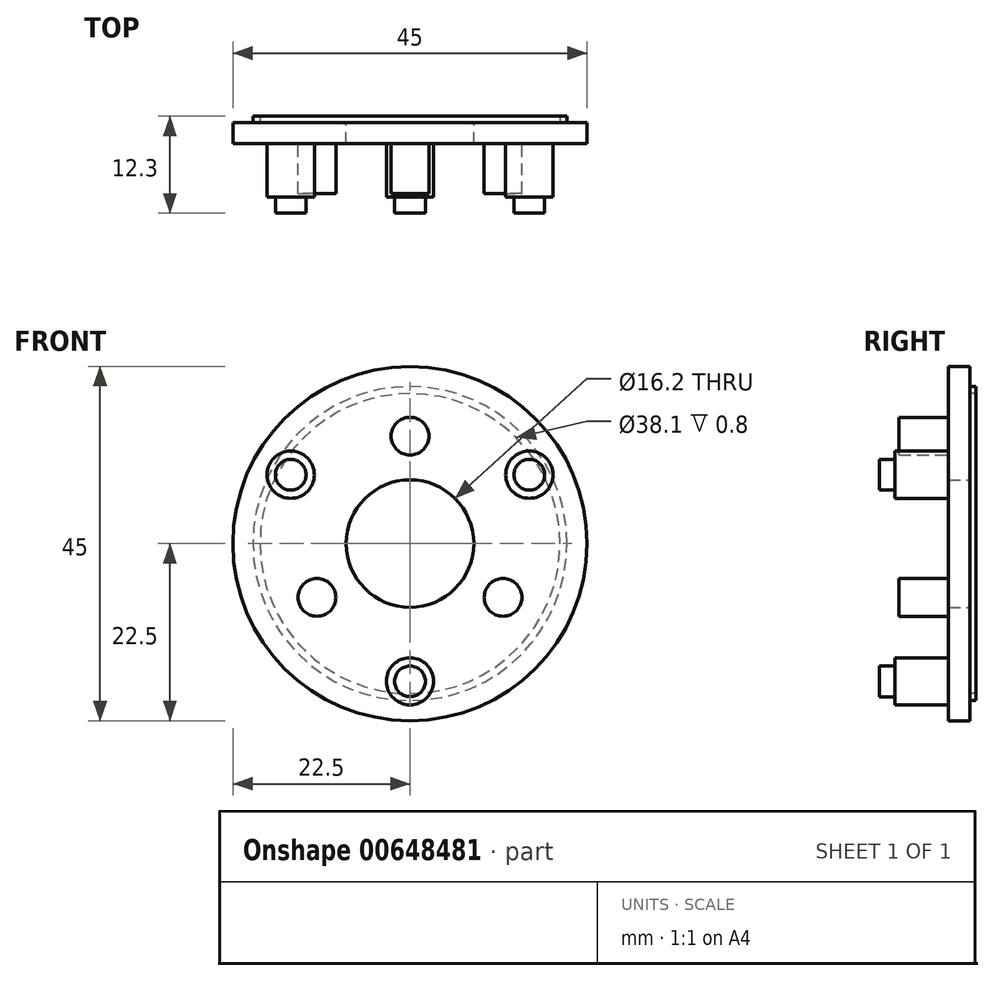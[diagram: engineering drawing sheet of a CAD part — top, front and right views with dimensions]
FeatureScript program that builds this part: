
annotation { "Feature Type Name" : "Feature", "Feature Type Description" : "" }
export const myFeature = defineFeature(function(context is Context, id is Id, definition is map)
    precondition{}
    {
        {
            var Q0;
            Q0=qCreatedBy(makeId("Front.planeOp"),FACE);
            var sketch = newSketch(context, id + "F0", { "sketchPlane" : qUnion([Q0])});
            skCircle(sketch, "E0", {"center": v(0, 0) * mm, "radius": 22.5 * mm});
            skCircle(sketch, "E1", {"center": v(0, 0) * mm, "radius": 8.1 * mm});
            skSolve(sketch);
        }
        {
            var Q0;
            Q0 = qSketchRegion(id + "F0", true);
            extrude(context, id + "F1", {"entities" : qUnion([Q0]), "depth" : 2.7 * mm, "offsetDistance" : 25 * mm});
        }
        {
            var Q0;
            Q0=makeQuery(id+"F1.opExtrude","CAP_FACE",FACE,{"disambiguationData":[OSD([sQuery(id+"F0.wireOp",EDGE,"E0"),sQuery(id+"F0.wireOp",EDGE,"E1")])],"isStart":false});
            var sketch = newSketch(context, id + "F2", { "sketchPlane" : qUnion([Q0])});
            skCircle(sketch, "E2", {"center": v(0, 13.65) * mm, "radius": 2.4 * mm});
            skCircle(sketch, "E3.1.0", {"center": v(-11.82, -6.82) * mm, "radius": 2.4 * mm});
            skCircle(sketch, "E3.2.0", {"center": v(11.82, -6.83) * mm, "radius": 2.4 * mm});
            skPoint(sketch, "E3.center", {"position": v(0, 0) * mm});
            skSolve(sketch);
        }
        {
            var Q0;
            Q0 = qSketchRegion(id + "F2", true);
            extrude(context, id + "F3", {"entities" : qUnion([Q0]), "operationType" : NewBodyOperationType.ADD, "depth" : 6.3 * mm, "offsetDistance" : 25 * mm});
        }
        {
            var Q0;
            Q0=makeQuery(id+"F1.opExtrude","CAP_FACE",FACE,{"disambiguationData":[OSD([sQuery(id+"F0.wireOp",EDGE,"E0"),sQuery(id+"F0.wireOp",EDGE,"E1")])],"isStart":false});
            var sketch = newSketch(context, id + "F4", { "sketchPlane" : qUnion([Q0])});
            skCircle(sketch, "E4", {"center": v(0, -17.5) * mm, "radius": 3 * mm});
            skCircle(sketch, "E5.1.0", {"center": v(15.16, 8.75) * mm, "radius": 3 * mm});
            skCircle(sketch, "E5.2.0", {"center": v(-15.16, 8.75) * mm, "radius": 3 * mm});
            skPoint(sketch, "E5.center", {"position": v(0, 0) * mm});
            skSolve(sketch);
        }
        {
            var Q0;
            Q0 = qSketchRegion(id + "F4", true);
            extrude(context, id + "F5", {"entities" : qUnion([Q0]), "operationType" : NewBodyOperationType.ADD, "depth" : 6.8 * mm, "offsetDistance" : 25 * mm});
        }
        {
            var Q0;
            Q0=makeQuery(id+"F5.opExtrude","CAP_FACE",FACE,{"disambiguationData":[OSD([sQuery(id+"F4.wireOp",EDGE,"E4")])],"isStart":false});
            var sketch = newSketch(context, id + "F6", { "sketchPlane" : qUnion([Q0])});
            skCircle(sketch, "E6", {"center": v(0, -17.5) * mm, "radius": 1.95 * mm});
            skSolve(sketch);
        }
        {
            var Q0;
            Q0=makeQuery(id+"F5.opExtrude","CAP_FACE",FACE,{"disambiguationData":[OSD([sQuery(id+"F4.wireOp",EDGE,"E5.2.0")])],"isStart":false});
            var sketch = newSketch(context, id + "F7", { "sketchPlane" : qUnion([Q0])});
            skCircle(sketch, "E7", {"center": v(-15.16, 8.75) * mm, "radius": 1.95 * mm});
            skSolve(sketch);
        }
        {
            var Q0;
            Q0=makeQuery(id+"F5.opExtrude","CAP_FACE",FACE,{"disambiguationData":[OSD([sQuery(id+"F4.wireOp",EDGE,"E5.1.0")])],"isStart":false});
            var sketch = newSketch(context, id + "F8", { "sketchPlane" : qUnion([Q0])});
            skCircle(sketch, "E8", {"center": v(15.16, 8.75) * mm, "radius": 1.95 * mm});
            skSolve(sketch);
        }
        {
            var Q0;
            Q0 = qSketchRegion(id + "F6", true);
            var Q1;
            Q1 = qSketchRegion(id + "F7", true);
            var Q2;
            Q2 = qSketchRegion(id + "F8", true);
            extrude(context, id + "F9", {"entities" : qUnion([Q0, Q1, Q2]), "operationType" : NewBodyOperationType.ADD, "depth" : 2 * mm, "offsetDistance" : 25 * mm});
        }
        {
            var Q0;
            Q0=makeQuery(id+"F1.opExtrude","CAP_FACE",FACE,{"disambiguationData":[OSD([sQuery(id+"F0.wireOp",EDGE,"E0"),sQuery(id+"F0.wireOp",EDGE,"E1")])],"isStart":true});
            var sketch = newSketch(context, id + "F10", { "sketchPlane" : qUnion([Q0])});
            skCircle(sketch, "E9", {"center": v(0, 0) * mm, "radius": 19.95 * mm});
            skCircle(sketch, "E10", {"center": v(0, 0) * mm, "radius": 19.05 * mm});
            skSolve(sketch);
        }
        {
            var Q0;
            Q0 = qSketchRegion(id + "F10", true);
            extrude(context, id + "F11", {"entities" : qUnion([Q0]), "operationType" : NewBodyOperationType.ADD, "depth" : 0.8 * mm, "offsetDistance" : 25 * mm});
        }
    });
